# Revit family: Drinking_Fountain-Oasis-Radii_Modular_Fountain-M140R
name_source: partatom
category: Plumbing Fixtures
revit_build: Autodesk Revit MEP 2013 (Build: 20130531_2115(x64)
units: mm (PartAtom-declared; Revit-internal decimal feet)

## types (1)
- M140R
    Base Rate = 0 GPM
    Chiller = No
    Default Elevation = 2' - 3"
    Description = Radii Modular Fountain
    Finish = Metal - Oasis International - Brushed Stainless Steel - Exterior Finish
    Manufacturer = Oasis International
    Manufacturer Fax Number = (614)322-4557
    Metal Finish = Metal - Oasis International - Brushed Stainless Steel - Exterior Finish
    Model = M140R
    Product Documentation Link = http://www.oasiscoolers.com
    Product Name = Non Refrigerated, Radii Fountain
    Product Page URL = http://www.oasiscoolers.com
    Rated Capacity = 0 GPM
    URL = http://www.oasiscoolers.com
    Width = 3' - 2 3/4"

## geometry (parser evidence)
native form markers: Blend x10, Sweep x15
no freeform markers — native parametric forms only
